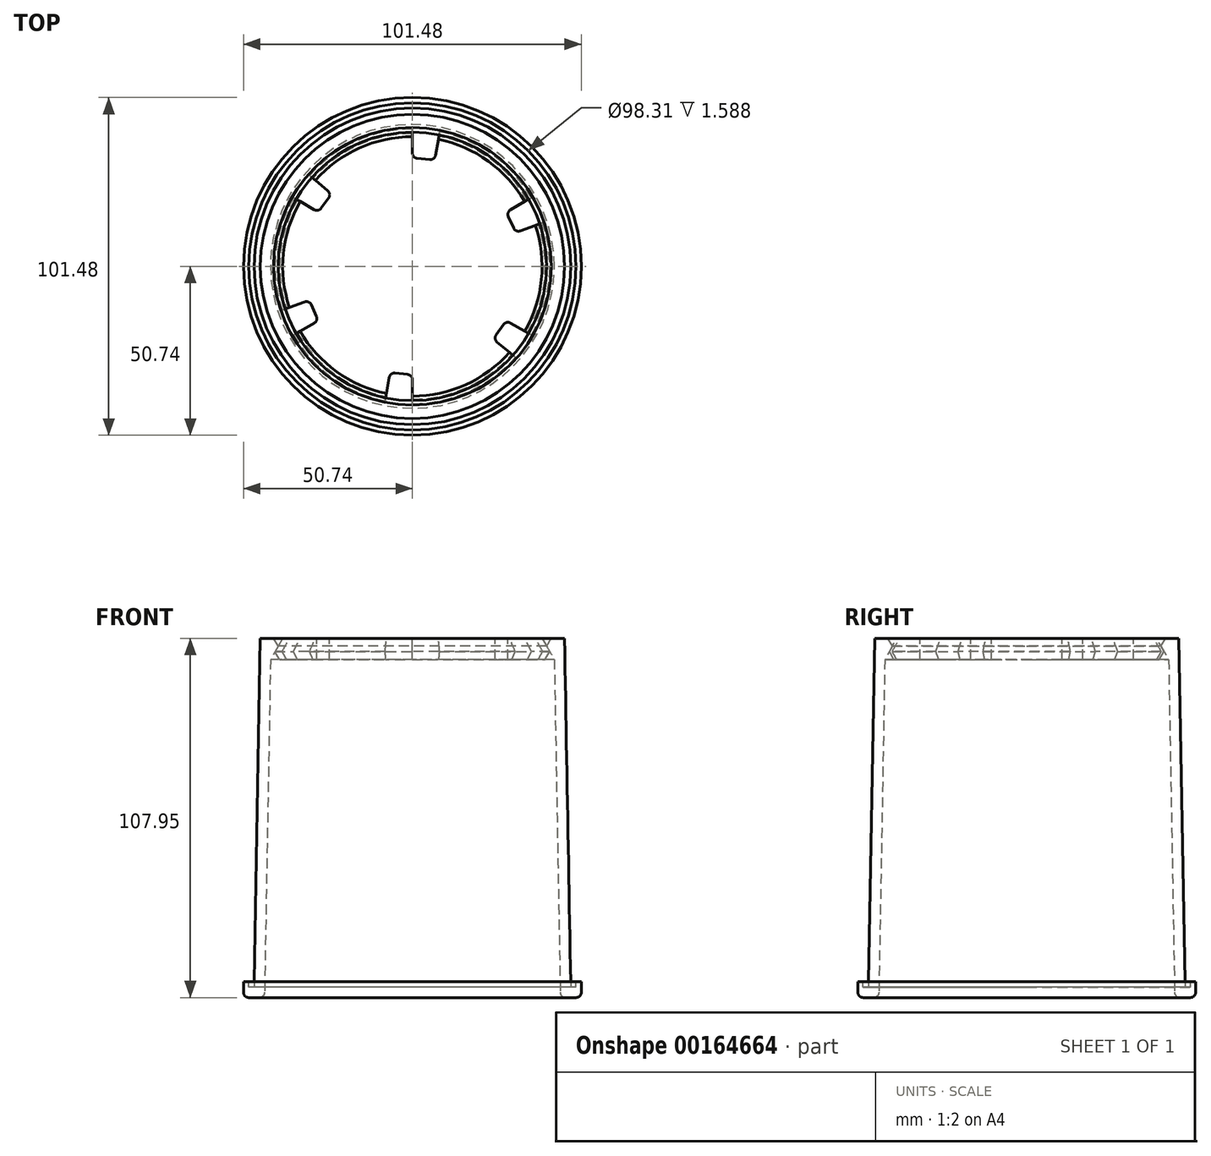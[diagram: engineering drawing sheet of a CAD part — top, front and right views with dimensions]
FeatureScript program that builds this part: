
annotation { "Feature Type Name" : "Feature", "Feature Type Description" : "" }
export const myFeature = defineFeature(function(context is Context, id is Id, definition is map)
    precondition{}
    {
        {
            var Q0;
            Q0=qCreatedBy(makeId("Front.planeOp"),FACE);
            var sketch = newSketch(context, id + "F0", { "sketchPlane" : qUnion([Q0])});
            skLineSegment(sketch, "E0", {"start": v(-44.45, 0) * mm, "end": v(-50.74, 0) * mm});
            skLineSegment(sketch, "E1", {"start": v(-50.74, 0) * mm, "end": v(-50.74, 4.76) * mm});
            skLineSegment(sketch, "E2", {"start": v(-50.74, 4.76) * mm, "end": v(-49.16, 4.76) * mm});
            skLineSegment(sketch, "E3", {"start": v(-49.16, 4.76) * mm, "end": v(-49.16, 3.17) * mm});
            skLineSegment(sketch, "E4", {"start": v(-49.16, 3.17) * mm, "end": v(-47.57, 3.18) * mm});
            skLineSegment(sketch, "E5", {"start": v(-47.57, 3.17) * mm, "end": v(-45.69, 107.95) * mm});
            skLineSegment(sketch, "E6", {"start": v(-45.69, 107.95) * mm, "end": v(-38.96, 107.95) * mm});
            skLineSegment(sketch, "E7", {"start": v(-38.96, 107.95) * mm, "end": v(-42.63, 101.6) * mm});
            skLineSegment(sketch, "E8", {"start": v(-42.63, 101.6) * mm, "end": v(-44.45, 0) * mm});
            skLineSegment(sketch, "E9", {"start": v(-38.96, 107.95) * mm, "end": v(0, 107.95) * mm});
            skLineSegment(sketch, "E10", {"start": v(0, 107.95) * mm, "end": v(0, 101.6) * mm});
            skLineSegment(sketch, "E11", {"start": v(0, 101.6) * mm, "end": v(-42.63, 101.6) * mm});
            skSolve(sketch);
        }
        {
            var Q0;
            Q0=makeQuery(id+"F0.imprint","IMPRINT",FACE,{"disambiguationData":[TD([[makeQuery(id+"F0.imprint","IMPRINT",EDGE,{"derivedFrom":sQuery(id+"F0.wireOp",EDGE,"E0")}),-1.0]])]});
            var Q1;
            Q1=sQuery(id+"F0.wireOp",EDGE,"E10");
            revolve(context, id + "F1", {"entities" : qUnion([Q0]), "axis" : qUnion([Q1]), "revolveType" : RevolveType.FULL});
        }
        {
            var Q0;
            Q0=makeQuery(id+"F0.imprint","IMPRINT",FACE,{"disambiguationData":[TD([[makeQuery(id+"F0.imprint","IMPRINT",EDGE,{"derivedFrom":sQuery(id+"F0.wireOp",EDGE,"E7")}),1.0]])]});
            var Q1;
            Q1=sQuery(id+"F0.wireOp",EDGE,"E10");
            revolve(context, id + "F2", {"entities" : qUnion([Q0]), "axis" : qUnion([Q1]), "revolveType" : RevolveType.FULL});
        }
        {
            var Q0;
            Q0=makeQuery(id+"F1.opRevolve","SWEPT_EDGE",EDGE,{"disambiguationData":[OSD([sQuery(id+"F0.wireOp",EDGE,"E6"),sQuery(id+"F0.wireOp",EDGE,"E7"),sQuery(id+"F0.wireOp",EDGE,"E9")])]});
            var Q1;
            Q1=makeQuery(id+"F2.opRevolve","SWEPT_EDGE",EDGE,{"disambiguationData":[OSD([sQuery(id+"F0.wireOp",EDGE,"E7"),sQuery(id+"F0.wireOp",EDGE,"E8"),sQuery(id+"F0.wireOp",EDGE,"E11")])]});
            chamfer(context, id + "F3", {"entities" : qUnion([Q0, Q1]), "width" : 1.59 * mm, "tangentPropagation" : true});
        }
        {
            var Q0;
            Q0=makeQuery(id+"F1.opRevolve","SWEPT_EDGE",EDGE,{"disambiguationData":[OSD([sQuery(id+"F0.wireOp",EDGE,"E0"),sQuery(id+"F0.wireOp",EDGE,"E8")])]});
            var Q1;
            Q1=makeQuery(id+"F1.opRevolve","SWEPT_EDGE",EDGE,{"disambiguationData":[OSD([sQuery(id+"F0.wireOp",EDGE,"E0"),sQuery(id+"F0.wireOp",EDGE,"E1")])]});
            fillet(context, id + "F4", {"entities" : qUnion([Q0, Q1]), "radius" : 1.59 * mm, "tangentPropagation" : true, "allowEdgeOverflow" : false});
        }
        {
            var Q0;
            Q0=makeQuery(id+"F2.opRevolve","SWEPT_FACE",FACE,{"disambiguationData":[OSD([sQuery(id+"F0.wireOp",EDGE,"E9")])]});
            var sketch = newSketch(context, id + "F5", { "sketchPlane" : qUnion([Q0])});
            skCircle(sketch, "E12.0", {"center": v(0, 0) * mm, "radius": 32.61 * mm, "construction": true});
            skCircle(sketch, "E13.0", {"center": v(0, 0) * mm, "radius": 45.31 * mm});
            skLineSegment(sketch, "E14", {"start": v(0, 34.04) * mm, "end": v(0, 51.44) * mm});
            skLineSegment(sketch, "E15", {"start": v(0, 51.44) * mm, "end": v(10.14, 51.44) * mm});
            skLineSegment(sketch, "E16", {"start": v(10.14, 51.44) * mm, "end": v(6.96, 33.37) * mm});
            skLineSegment(sketch, "E17", {"start": v(5.23, 32.07) * mm, "end": v(1.42, 32.46) * mm});
            skPoint(sketch, "E18.visualSharp", {"position": v(0, 32.61) * mm});
            skArc(sketch, "E18.filletArc", {"start": v(0, 34.04) * mm, "mid": v(0.4, 32.98) * mm, "end": v(1.42, 32.46) * mm});
            skPoint(sketch, "E19.visualSharp", {"position": v(6.7, 31.92) * mm});
            skArc(sketch, "E19.filletArc", {"start": v(5.23, 32.07) * mm, "mid": v(6.35, 32.38) * mm, "end": v(6.96, 33.37) * mm});
            skSolve(sketch);
        }
        {
            var Q0;
            {var subQ0=sQuery(id+"F5.wireOp",EDGE,"E14");var subQ1=sQuery(id+"F5.wireOp",EDGE,"E13.0");var subQ2=makeQuery(id+"F5.imprint","INTERSECT",VERTEX,{"derivedFrom":[subQ1,subQ0]});Q0=makeQuery(id+"F5.imprint","IMPRINT",FACE,{"disambiguationData":[TD([[makeQuery(id+"F5.imprint","IMPRINT",EDGE,{"disambiguationData":[TD([[subQ2,1.0]])],"derivedFrom":subQ1}),1.0]])]});}
            var Q1;
            Q1=makeQuery(id+"F5.imprint","IMPRINT",FACE,{"disambiguationData":[TD([[makeQuery(id+"F5.imprint","IMPRINT",EDGE,{"derivedFrom":sQuery(id+"F5.wireOp",EDGE,"E17")}),-1.0]])]});
            extrude(context, id + "F6", {"entities" : qUnion([Q0, Q1]), "oppositeDirection" : true, "depth" : 25.4 * mm});
        }
        {
            var Q0;
            Q0=makeQuery(id+"F6.opExtrude","SWEPT_BODY",BODY,{"disambiguationData":[OSD([sQuery(id+"F5.wireOp",EDGE,"E13.0"),sQuery(id+"F5.wireOp",EDGE,"E14"),sQuery(id+"F5.wireOp",EDGE,"E16"),sQuery(id+"F5.wireOp",EDGE,"E17"),sQuery(id+"F5.wireOp",EDGE,"E18.filletArc"),sQuery(id+"F5.wireOp",EDGE,"E19.filletArc")])]});
            var Q1;
            Q1=sQuery(id+"F0.wireOp",EDGE,"E10");
            circularPattern(context, id + "F7", {"entities" : qUnion([Q0]), "axis" : qUnion([Q1]), "angle" : 360 * degree, "instanceCount" : 6, "equalSpace" : true});
        }
        {
            var Q0;
            Q0=makeQuery(id+"F7.opPattern","COPY",BODY,{"derivedFrom":makeQuery(id+"F6.opExtrude","SWEPT_BODY",BODY,{"disambiguationData":[OSD([sQuery(id+"F5.wireOp",EDGE,"E13.0"),sQuery(id+"F5.wireOp",EDGE,"E14"),sQuery(id+"F5.wireOp",EDGE,"E16"),sQuery(id+"F5.wireOp",EDGE,"E17"),sQuery(id+"F5.wireOp",EDGE,"E18.filletArc"),sQuery(id+"F5.wireOp",EDGE,"E19.filletArc")])]}),"instanceName":"4"});
            var Q1;
            Q1=makeQuery(id+"F7.opPattern","COPY",BODY,{"derivedFrom":makeQuery(id+"F6.opExtrude","SWEPT_BODY",BODY,{"disambiguationData":[OSD([sQuery(id+"F5.wireOp",EDGE,"E13.0"),sQuery(id+"F5.wireOp",EDGE,"E14"),sQuery(id+"F5.wireOp",EDGE,"E16"),sQuery(id+"F5.wireOp",EDGE,"E17"),sQuery(id+"F5.wireOp",EDGE,"E18.filletArc"),sQuery(id+"F5.wireOp",EDGE,"E19.filletArc")])]}),"instanceName":"3"});
            var Q2;
            Q2=makeQuery(id+"F7.opPattern","COPY",BODY,{"derivedFrom":makeQuery(id+"F6.opExtrude","SWEPT_BODY",BODY,{"disambiguationData":[OSD([sQuery(id+"F5.wireOp",EDGE,"E13.0"),sQuery(id+"F5.wireOp",EDGE,"E14"),sQuery(id+"F5.wireOp",EDGE,"E16"),sQuery(id+"F5.wireOp",EDGE,"E17"),sQuery(id+"F5.wireOp",EDGE,"E18.filletArc"),sQuery(id+"F5.wireOp",EDGE,"E19.filletArc")])]}),"instanceName":"2"});
            var Q3;
            Q3=makeQuery(id+"F7.opPattern","COPY",BODY,{"derivedFrom":makeQuery(id+"F6.opExtrude","SWEPT_BODY",BODY,{"disambiguationData":[OSD([sQuery(id+"F5.wireOp",EDGE,"E13.0"),sQuery(id+"F5.wireOp",EDGE,"E14"),sQuery(id+"F5.wireOp",EDGE,"E16"),sQuery(id+"F5.wireOp",EDGE,"E17"),sQuery(id+"F5.wireOp",EDGE,"E18.filletArc"),sQuery(id+"F5.wireOp",EDGE,"E19.filletArc")])]}),"instanceName":"1"});
            var Q4;
            Q4=makeQuery(id+"F6.opExtrude","SWEPT_BODY",BODY,{"disambiguationData":[OSD([sQuery(id+"F5.wireOp",EDGE,"E13.0"),sQuery(id+"F5.wireOp",EDGE,"E14"),sQuery(id+"F5.wireOp",EDGE,"E16"),sQuery(id+"F5.wireOp",EDGE,"E17"),sQuery(id+"F5.wireOp",EDGE,"E18.filletArc"),sQuery(id+"F5.wireOp",EDGE,"E19.filletArc")])]});
            var Q5;
            Q5=makeQuery(id+"F7.opPattern","COPY",BODY,{"derivedFrom":makeQuery(id+"F6.opExtrude","SWEPT_BODY",BODY,{"disambiguationData":[OSD([sQuery(id+"F5.wireOp",EDGE,"E13.0"),sQuery(id+"F5.wireOp",EDGE,"E14"),sQuery(id+"F5.wireOp",EDGE,"E16"),sQuery(id+"F5.wireOp",EDGE,"E17"),sQuery(id+"F5.wireOp",EDGE,"E18.filletArc"),sQuery(id+"F5.wireOp",EDGE,"E19.filletArc")])]}),"instanceName":"5"});
            var Q6;
            Q6=makeQuery(id+"F2.opRevolve","SWEPT_BODY",BODY,{"disambiguationData":[OSD([sQuery(id+"F0.wireOp",EDGE,"E7"),sQuery(id+"F0.wireOp",EDGE,"E9"),sQuery(id+"F0.wireOp",EDGE,"E10"),sQuery(id+"F0.wireOp",EDGE,"E11")])]});
            booleanBodies(context, id + "F8", {"operationType" : BooleanOperationType.SUBTRACTION, "tools" : qUnion([Q0, Q1, Q2, Q3, Q4, Q5]), "targets" : qUnion([Q6])});
        }
    });
